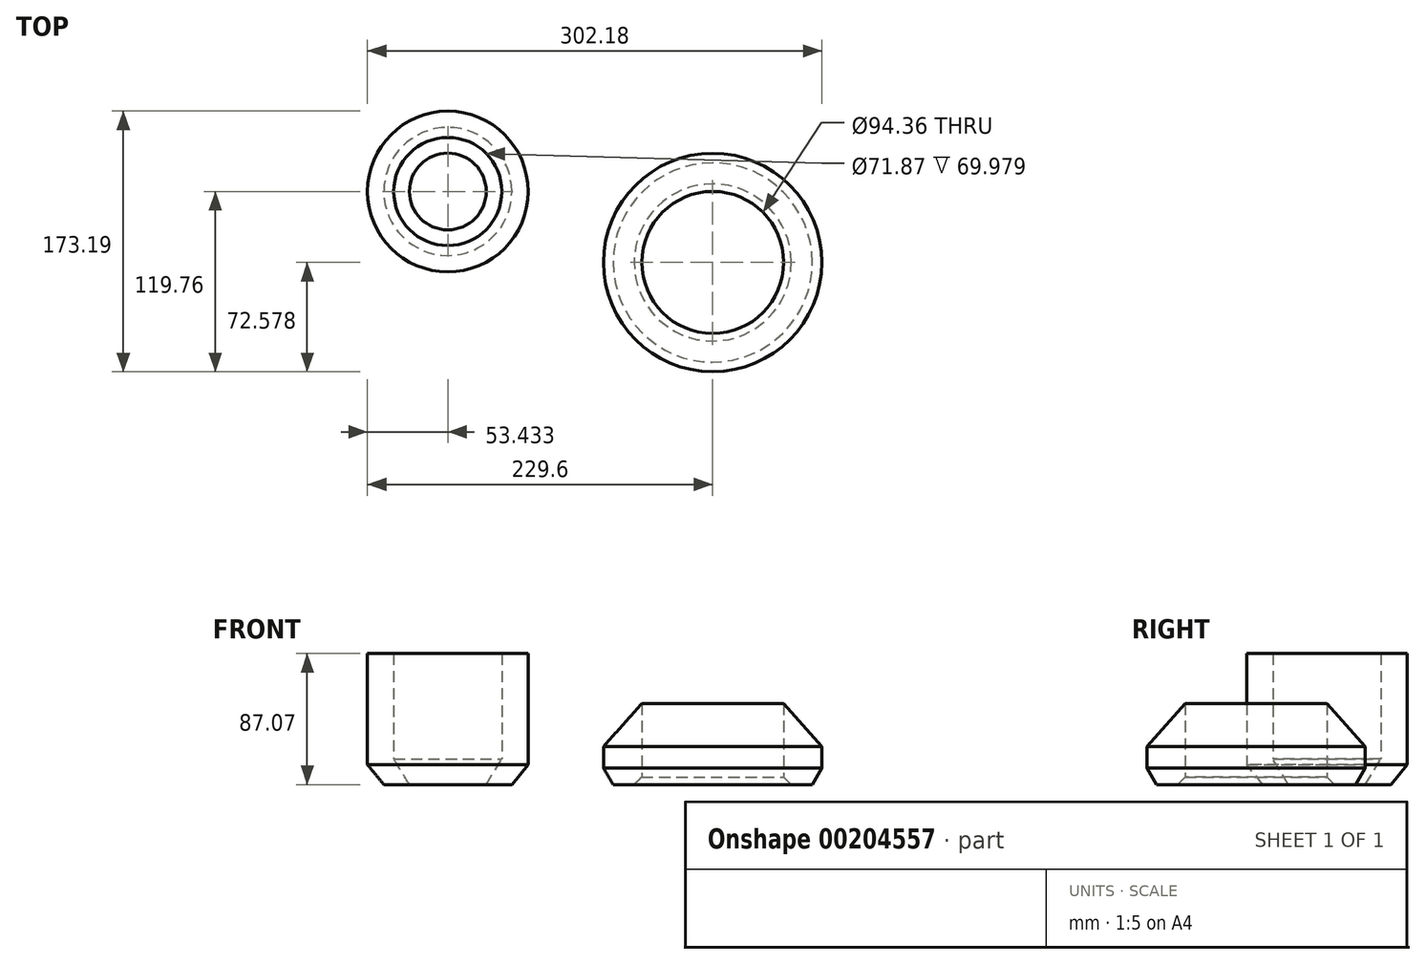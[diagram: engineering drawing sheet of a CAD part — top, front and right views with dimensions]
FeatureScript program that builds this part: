
annotation { "Feature Type Name" : "Feature", "Feature Type Description" : "" }
export const myFeature = defineFeature(function(context is Context, id is Id, definition is map)
    precondition{}
    {
        {
            var Q0;
            Q0=qCreatedBy(makeId("Front.planeOp"),FACE);
            var sketch = newSketch(context, id + "F0", { "sketchPlane" : qUnion([Q0])});
            skLineSegment(sketch, "E0.bottom", {"start": v(0, 0) * mm, "end": v(-50.8, 0) * mm});
            skLineSegment(sketch, "E0.top", {"start": v(0, 50.8) * mm, "end": v(-50.8, 50.8) * mm});
            skLineSegment(sketch, "E0.left", {"start": v(0, 0) * mm, "end": v(0, 50.8) * mm});
            skLineSegment(sketch, "E0.right", {"start": v(-50.8, 0) * mm, "end": v(-50.8, 50.8) * mm});
            skSolve(sketch);
        }
        {
            var Q0;
            Q0=qCreatedBy(makeId("Front.planeOp"),FACE);
            var sketch = newSketch(context, id + "F1", { "sketchPlane" : qUnion([Q0])});
            skLineSegment(sketch, "E1", {"start": v(-25.4, 50.9) * mm, "end": v(-25.4, 177.9) * mm, "construction": true});
            skLineSegment(sketch, "E2", {"start": v(-25.4, 50.9) * mm, "end": v(0, 50.9) * mm});
            skLineSegment(sketch, "E3", {"start": v(0, 50.9) * mm, "end": v(0, 59.36) * mm});
            skLineSegment(sketch, "E4", {"start": v(-25.4, 50.9) * mm, "end": v(-25.4, 177.9) * mm});
            skLineSegment(sketch, "E5", {"start": v(0, 59.36) * mm, "end": v(-12.7, 70.43) * mm});
            skPoint(sketch, "E5.endSnap0", {"position": v(-12.7, 50.9) * mm});
            skLineSegment(sketch, "E6", {"start": v(-12.7, 70.43) * mm, "end": v(-3.48, 79.88) * mm});
            skLineSegment(sketch, "E7", {"start": v(-3.48, 79.88) * mm, "end": v(3, 133.35) * mm});
            skLineSegment(sketch, "E8", {"start": v(3, 133.35) * mm, "end": v(-13.85, 147.2) * mm});
            skLineSegment(sketch, "E9", {"start": v(-13.85, 147.2) * mm, "end": v(0, 164.05) * mm});
            skLineSegment(sketch, "E10", {"start": v(0, 164.05) * mm, "end": v(-16.85, 177.9) * mm});
            skLineSegment(sketch, "E11", {"start": v(-16.85, 177.9) * mm, "end": v(-25.4, 177.9) * mm});
            skSolve(sketch);
        }
        {
            var Q0;
            Q0=qCreatedBy(makeId("Top.planeOp"),FACE);
            var sketch = newSketch(context, id + "F2", { "sketchPlane" : qUnion([Q0])});
            skLineSegment(sketch, "E12", {"start": v(0, -26.97) * mm, "end": v(0, 40.68) * mm, "construction": true});
            skSolve(sketch);
        }
        {
            var Q0;
            Q0=qCreatedBy(makeId("Right.planeOp"),FACE);
            var sketch = newSketch(context, id + "F3", { "sketchPlane" : qUnion([Q0])});
            skLineSegment(sketch, "E13.bottom", {"start": v(0, 0) * mm, "end": v(25.4, 0) * mm});
            skLineSegment(sketch, "E13.top", {"start": v(0, 25.4) * mm, "end": v(25.4, 25.4) * mm, "construction": true});
            skLineSegment(sketch, "E13.left", {"start": v(0, 0) * mm, "end": v(0, 25.4) * mm});
            skLineSegment(sketch, "E13.right", {"start": v(25.4, 0) * mm, "end": v(25.4, 25.4) * mm});
            skLineSegment(sketch, "E14", {"start": v(0, 25.4) * mm, "end": v(0, 53.8) * mm});
            skLineSegment(sketch, "E15", {"start": v(0, 53.8) * mm, "end": v(25.4, 25.4) * mm});
            skLineSegment(sketch, "E16", {"start": v(0, 0) * mm, "end": v(0, 84.17) * mm, "construction": true});
            skPoint(sketch, "E16.endSnap0", {"position": v(0, 39.6) * mm});
            skLineSegment(sketch, "E17", {"start": v(-47.18, 0) * mm, "end": v(-47.18, 87.47) * mm, "construction": true});
            skSolve(sketch);
        }
        {
            var Q0;
            Q0=makeQuery(id+"F3.imprint","IMPRINT",FACE,{"disambiguationData":[TD([[makeQuery(id+"F3.imprint","IMPRINT",EDGE,{"derivedFrom":sQuery(id+"F3.wireOp",EDGE,"E13.bottom")}),1.0]])]});
            var Q1;
            Q1=sQuery(id+"F3.wireOp",EDGE,"E17");
            revolve(context, id + "F4", {"entities" : qUnion([Q0]), "axis" : qUnion([Q1]), "revolveType" : RevolveType.FULL});
        }
        {
            var Q0;
            Q0=makeQuery(id+"F4.opRevolve","SWEPT_EDGE",EDGE,{"disambiguationData":[OSD([sQuery(id+"F3.wireOp",EDGE,"E13.bottom"),sQuery(id+"F3.wireOp",EDGE,"E13.right")])]});
            chamfer(context, id + "F5", {"entities" : qUnion([Q0]), "chamferType" : ChamferType.OFFSET_ANGLE, "width" : 6.35 * mm, "oppositeDirection" : false, "angle" : 60 * degree, "tangentPropagation" : true});
        }
        {
            var Q0;
            Q0=makeQuery(id+"F4.opRevolve","SWEPT_EDGE",EDGE,{"disambiguationData":[OSD([sQuery(id+"F3.wireOp",EDGE,"E13.bottom"),sQuery(id+"F3.wireOp",EDGE,"E13.left")])]});
            chamfer(context, id + "F6", {"entities" : qUnion([Q0]), "chamferType" : ChamferType.OFFSET_ANGLE, "width" : 5.08 * mm, "oppositeDirection" : false, "angle" : 45 * degree, "tangentPropagation" : true});
        }
        {
            var Q0;
            Q0=qCreatedBy(makeId("Front.planeOp"),FACE);
            var sketch = newSketch(context, id + "F7", { "sketchPlane" : qUnion([Q0])});
            skLineSegment(sketch, "E18", {"start": v(-150.63, 0) * mm, "end": v(-133.61, 0) * mm});
            skLineSegment(sketch, "E19", {"start": v(-133.61, 0) * mm, "end": v(-122.74, 13.3) * mm});
            skLineSegment(sketch, "E20", {"start": v(-122.74, 13.3) * mm, "end": v(-122.74, 87.07) * mm});
            skLineSegment(sketch, "E21", {"start": v(-122.74, 87.07) * mm, "end": v(-140.23, 87.07) * mm});
            skLineSegment(sketch, "E22", {"start": v(-140.23, 87.07) * mm, "end": v(-140.23, 17.09) * mm});
            skLineSegment(sketch, "E23", {"start": v(-140.23, 17.09) * mm, "end": v(-150.63, 0) * mm});
            skLineSegment(sketch, "E24", {"start": v(-176.17, 0) * mm, "end": v(-176.17, 103.62) * mm, "construction": true});
            skSolve(sketch);
        }
        {
            var Q0;
            Q0 = qSketchRegion(id + "F7", true);
            var Q1;
            Q1=sQuery(id+"F7.wireOp",EDGE,"E24");
            revolve(context, id + "F8", {"entities" : qUnion([Q0]), "axis" : qUnion([Q1]), "revolveType" : RevolveType.FULL});
        }
    });
